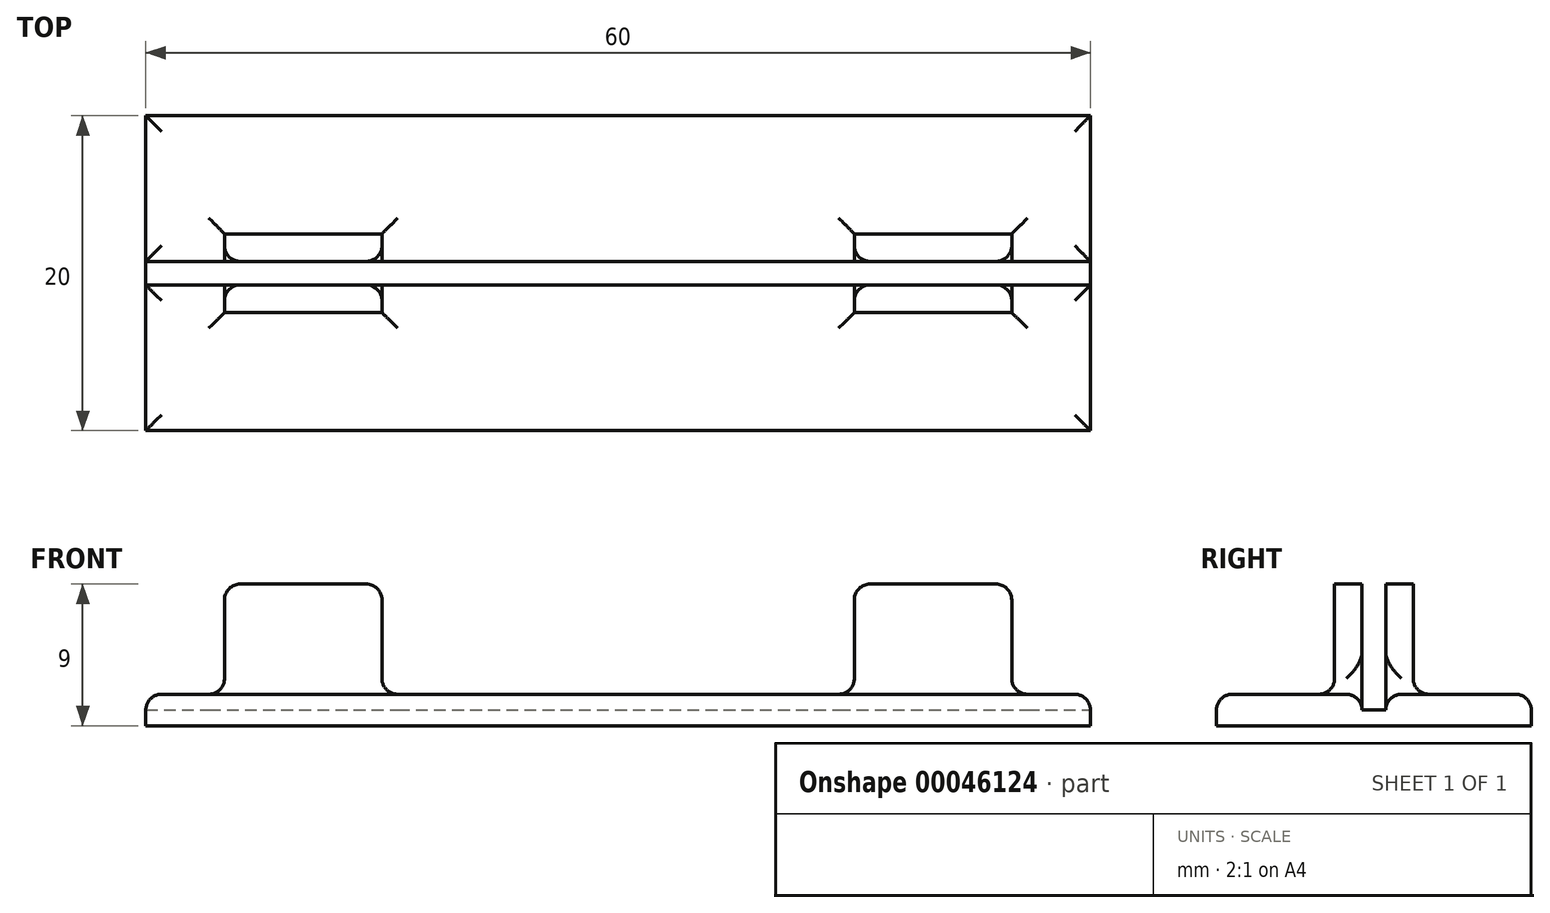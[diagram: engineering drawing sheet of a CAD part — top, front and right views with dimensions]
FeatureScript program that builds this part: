
annotation { "Feature Type Name" : "Feature", "Feature Type Description" : "" }
export const myFeature = defineFeature(function(context is Context, id is Id, definition is map)
    precondition{}
    {
        {
            var Q0;
            Q0=qCreatedBy(makeId("Top.planeOp"),FACE);
            var sketch = newSketch(context, id + "F0", { "sketchPlane" : qUnion([Q0])});
            skLineSegment(sketch, "E0.rect.bottom", {"start": v(-30, -10) * mm, "end": v(30, -10) * mm});
            skLineSegment(sketch, "E0.rect.top", {"start": v(-30, 10) * mm, "end": v(30, 10) * mm});
            skLineSegment(sketch, "E0.rect.left", {"start": v(-30, -10) * mm, "end": v(-30, 10) * mm});
            skLineSegment(sketch, "E0.rect.right", {"start": v(30, -10) * mm, "end": v(30, 10) * mm});
            skPoint(sketch, "E0.rect.middle", {"position": v(0, 0) * mm});
            skSolve(sketch);
        }
        {
            var Q0;
            Q0 = qSketchRegion(id + "F0", true);
            extrude(context, id + "F1", {"entities" : qUnion([Q0]), "depth" : 2 * mm});
        }
        {
            var Q0;
            Q0=makeQuery(id+"F1.opExtrude","CAP_FACE",FACE,{"disambiguationData":[OSD([sQuery(id+"F0.wireOp",EDGE,"E0.rect.bottom"),sQuery(id+"F0.wireOp",EDGE,"E0.rect.top"),sQuery(id+"F0.wireOp",EDGE,"E0.rect.left"),sQuery(id+"F0.wireOp",EDGE,"E0.rect.right")])],"isStart":false});
            var sketch = newSketch(context, id + "F2", { "sketchPlane" : qUnion([Q0])});
            skLineSegment(sketch, "E1", {"start": v(0, 0) * mm, "end": v(-20, 0) * mm, "construction": true});
            skLineSegment(sketch, "E2.rect.bottom", {"start": v(-25, 2.5) * mm, "end": v(-15, 2.5) * mm});
            skLineSegment(sketch, "E2.rect.top", {"start": v(-25, -2.5) * mm, "end": v(-15, -2.5) * mm});
            skLineSegment(sketch, "E2.rect.left", {"start": v(-25, 2.5) * mm, "end": v(-25, -2.5) * mm});
            skLineSegment(sketch, "E2.rect.right", {"start": v(-15, 2.5) * mm, "end": v(-15, -2.5) * mm});
            skPoint(sketch, "E2.rect.middle", {"position": v(-20, 0) * mm});
            skLineSegment(sketch, "E3", {"start": v(0, 0) * mm, "end": v(0, 2.5) * mm, "construction": true});
            skLineSegment(sketch, "E4.MirrorCS", {"start": v(15, 2.5) * mm, "end": v(15, -2.5) * mm});
            skLineSegment(sketch, "E5.MirrorCS", {"start": v(25, 2.5) * mm, "end": v(15, 2.5) * mm});
            skLineSegment(sketch, "E6.MirrorCS", {"start": v(25, 2.5) * mm, "end": v(25, -2.5) * mm});
            skLineSegment(sketch, "E7.MirrorCS", {"start": v(25, -2.5) * mm, "end": v(15, -2.5) * mm});
            skSolve(sketch);
        }
        {
            var Q0;
            Q0=makeQuery(id+"F2.imprint","IMPRINT",FACE,{"disambiguationData":[TD([[makeQuery(id+"F2.imprint","IMPRINT",EDGE,{"derivedFrom":sQuery(id+"F2.wireOp",EDGE,"E2.rect.bottom")}),-1.0]])]});
            var Q1;
            Q1=makeQuery(id+"F2.imprint","IMPRINT",FACE,{"disambiguationData":[TD([[makeQuery(id+"F2.imprint","IMPRINT",EDGE,{"derivedFrom":sQuery(id+"F2.wireOp",EDGE,"E4.MirrorCS")}),1.0]])]});
            extrude(context, id + "F3", {"entities" : qUnion([Q0, Q1]), "operationType" : NewBodyOperationType.ADD, "depth" : 7 * mm});
        }
        {
            var Q0;
            Q0=makeQuery(id+"F3.opExtrude","CAP_FACE",FACE,{"disambiguationData":[OSD([sQuery(id+"F2.wireOp",EDGE,"E2.rect.bottom"),sQuery(id+"F2.wireOp",EDGE,"E2.rect.top"),sQuery(id+"F2.wireOp",EDGE,"E2.rect.left"),sQuery(id+"F2.wireOp",EDGE,"E2.rect.right")])],"isStart":false});
            var sketch = newSketch(context, id + "F4", { "sketchPlane" : qUnion([Q0])});
            skLineSegment(sketch, "E8.0", {"start": v(-30, -10) * mm, "end": v(-30, 10) * mm, "construction": true});
            skLineSegment(sketch, "E9.rect.bottom", {"start": v(-30, 0.75) * mm, "end": v(30, 0.75) * mm});
            skLineSegment(sketch, "E9.rect.top", {"start": v(-30, -0.75) * mm, "end": v(30, -0.75) * mm});
            skLineSegment(sketch, "E9.rect.left", {"start": v(-30, 0.75) * mm, "end": v(-30, -0.75) * mm});
            skLineSegment(sketch, "E9.rect.right", {"start": v(30, 0.75) * mm, "end": v(30, -0.75) * mm});
            skPoint(sketch, "E9.rect.middle", {"position": v(0, 0) * mm});
            skSolve(sketch);
        }
        {
            var Q0;
            Q0 = qSketchRegion(id + "F4", true);
            extrude(context, id + "F5", {"entities" : qUnion([Q0]), "operationType" : NewBodyOperationType.REMOVE, "oppositeDirection" : true, "depth" : 8 * mm});
        }
        {
            var Q0;
            {var subQ0=sQuery(id+"F2.wireOp",EDGE,"E2.rect.right");var subQ1=sQuery(id+"F2.wireOp",EDGE,"E2.rect.bottom");Q0=makeQuery(id+"F5.boolean.opBoolean","SPLIT",EDGE,{"disambiguationData":[TD([makeQuery(id+"F3.opExtrude","SWEPT_FACE",FACE,{"disambiguationData":[OSD([subQ1])]})])],"derivedFrom":makeQuery(id+"F3.opExtrude","CAP_EDGE",EDGE,{"disambiguationData":[OSD([subQ0])],"isStart":false})});}
            var Q1;
            {var subQ0=sQuery(id+"F2.wireOp",EDGE,"E2.rect.left");var subQ1=sQuery(id+"F2.wireOp",EDGE,"E2.rect.bottom");Q1=makeQuery(id+"F5.boolean.opBoolean","SPLIT",EDGE,{"disambiguationData":[TD([makeQuery(id+"F3.opExtrude","SWEPT_FACE",FACE,{"disambiguationData":[OSD([subQ1])]})])],"derivedFrom":makeQuery(id+"F3.opExtrude","CAP_EDGE",EDGE,{"disambiguationData":[OSD([subQ0])],"isStart":false})});}
            var Q2;
            {var subQ0=sQuery(id+"F2.wireOp",EDGE,"E2.rect.left");var subQ1=sQuery(id+"F2.wireOp",EDGE,"E2.rect.top");Q2=makeQuery(id+"F5.boolean.opBoolean","SPLIT",EDGE,{"disambiguationData":[TD([makeQuery(id+"F3.opExtrude","SWEPT_FACE",FACE,{"disambiguationData":[OSD([subQ1])]})])],"derivedFrom":makeQuery(id+"F3.opExtrude","CAP_EDGE",EDGE,{"disambiguationData":[OSD([subQ0])],"isStart":false})});}
            var Q3;
            {var subQ0=sQuery(id+"F2.wireOp",EDGE,"E2.rect.right");var subQ1=sQuery(id+"F2.wireOp",EDGE,"E2.rect.top");Q3=makeQuery(id+"F5.boolean.opBoolean","SPLIT",EDGE,{"disambiguationData":[TD([makeQuery(id+"F3.opExtrude","SWEPT_FACE",FACE,{"disambiguationData":[OSD([subQ1])]})])],"derivedFrom":makeQuery(id+"F3.opExtrude","CAP_EDGE",EDGE,{"disambiguationData":[OSD([subQ0])],"isStart":false})});}
            var Q4;
            {var subQ0=sQuery(id+"F2.wireOp",EDGE,"E4.MirrorCS");var subQ1=sQuery(id+"F2.wireOp",EDGE,"E5.MirrorCS");Q4=makeQuery(id+"F5.boolean.opBoolean","SPLIT",EDGE,{"disambiguationData":[TD([makeQuery(id+"F3.opExtrude","SWEPT_FACE",FACE,{"disambiguationData":[OSD([subQ1])]})])],"derivedFrom":makeQuery(id+"F3.opExtrude","CAP_EDGE",EDGE,{"disambiguationData":[OSD([subQ0])],"isStart":false})});}
            var Q5;
            {var subQ0=sQuery(id+"F2.wireOp",EDGE,"E4.MirrorCS");var subQ1=sQuery(id+"F2.wireOp",EDGE,"E7.MirrorCS");Q5=makeQuery(id+"F5.boolean.opBoolean","SPLIT",EDGE,{"disambiguationData":[TD([makeQuery(id+"F3.opExtrude","SWEPT_FACE",FACE,{"disambiguationData":[OSD([subQ1])]})])],"derivedFrom":makeQuery(id+"F3.opExtrude","CAP_EDGE",EDGE,{"disambiguationData":[OSD([subQ0])],"isStart":false})});}
            var Q6;
            {var subQ0=sQuery(id+"F2.wireOp",EDGE,"E6.MirrorCS");var subQ1=sQuery(id+"F2.wireOp",EDGE,"E5.MirrorCS");Q6=makeQuery(id+"F5.boolean.opBoolean","SPLIT",EDGE,{"disambiguationData":[TD([makeQuery(id+"F3.opExtrude","SWEPT_FACE",FACE,{"disambiguationData":[OSD([subQ1])]})])],"derivedFrom":makeQuery(id+"F3.opExtrude","CAP_EDGE",EDGE,{"disambiguationData":[OSD([subQ0])],"isStart":false})});}
            var Q7;
            {var subQ0=sQuery(id+"F2.wireOp",EDGE,"E6.MirrorCS");var subQ1=sQuery(id+"F2.wireOp",EDGE,"E7.MirrorCS");Q7=makeQuery(id+"F5.boolean.opBoolean","SPLIT",EDGE,{"disambiguationData":[TD([makeQuery(id+"F3.opExtrude","SWEPT_FACE",FACE,{"disambiguationData":[OSD([subQ1])]})])],"derivedFrom":makeQuery(id+"F3.opExtrude","CAP_EDGE",EDGE,{"disambiguationData":[OSD([subQ0])],"isStart":false})});}
            var Q8;
            {var subQ0=sQuery(id+"F0.wireOp",EDGE,"E0.rect.bottom");var subQ1=sQuery(id+"F0.wireOp",EDGE,"E0.rect.left");var subQ2=sQuery(id+"F0.wireOp",EDGE,"E0.rect.right");Q8=makeQuery(id+"F5.boolean.opBoolean","SPLIT",FACE,{"disambiguationData":[TD([makeQuery(id+"F1.opExtrude","SWEPT_FACE",FACE,{"disambiguationData":[OSD([subQ0])]})])],"derivedFrom":makeQuery(id+"F1.opExtrude","CAP_FACE",FACE,{"disambiguationData":[OSD([subQ0,sQuery(id+"F0.wireOp",EDGE,"E0.rect.top"),subQ1,subQ2])],"isStart":false})});}
            var Q9;
            {var subQ0=sQuery(id+"F0.wireOp",EDGE,"E0.rect.top");var subQ1=sQuery(id+"F0.wireOp",EDGE,"E0.rect.left");var subQ2=sQuery(id+"F0.wireOp",EDGE,"E0.rect.right");Q9=makeQuery(id+"F5.boolean.opBoolean","SPLIT",FACE,{"disambiguationData":[TD([makeQuery(id+"F1.opExtrude","SWEPT_FACE",FACE,{"disambiguationData":[OSD([subQ0])]})])],"derivedFrom":makeQuery(id+"F1.opExtrude","CAP_FACE",FACE,{"disambiguationData":[OSD([sQuery(id+"F0.wireOp",EDGE,"E0.rect.bottom"),subQ0,subQ1,subQ2])],"isStart":false})});}
            fillet(context, id + "F6", {"entities" : qUnion([Q0, Q1, Q2, Q3, Q4, Q5, Q6, Q7, Q8, Q9]), "radius" : 1 * mm, "tangentPropagation" : true, "allowEdgeOverflow" : false});
        }
    });
